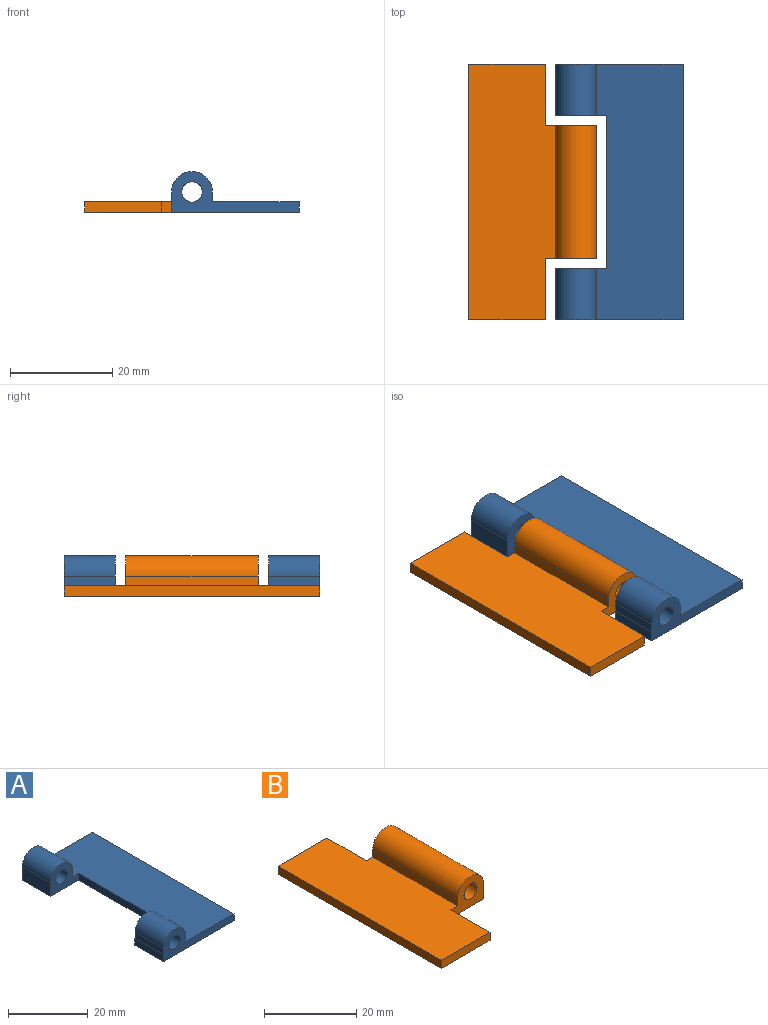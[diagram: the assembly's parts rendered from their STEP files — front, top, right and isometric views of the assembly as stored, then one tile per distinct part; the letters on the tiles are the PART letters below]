
ASSEMBLY  parts=2 mates=1
PART A: 18 faces, bbox 25x50x8 mm
  f0: plane 50x25.03mm, normal (0,0,-1), area 950.3mm2, adj f3,f5,f6,f7,f12,f13,f14,f15
  f1: plane 10x1.87mm, normal (1,0,0), area 18.6mm2, adj f2,f5,f8,f13
  f2: cylinder r=4mm len=10mm, axis (0,1,0), area 125.7mm2, adj f1,f5,f11,f13
  f3: plane 10x4mm, normal (-1,0,0), area 40mm2, adj f0,f6,f10,f12
  f4: plane 10x0.03mm, normal (0,0,1), area 0.3mm2, adj f5,f11,f13,f14
  f5: plane 25.03x8mm, normal (0,-1,0), area 80.9mm2, adj f0,f1,f2,f4,f7,f8,f11,f14
  f6: plane 25x8mm, normal (0,1,0), area 80.9mm2, adj f0,f3,f7,f8,f9,f10,f17
  f7: plane 50x2.14mm, normal (1,0,0), area 106.8mm2, adj f0,f5,f6,f8
  f8: plane 50x17mm, normal (0,0,1), area 790mm2, adj f1,f5,f6,f7,f9,f12,f13,f15
  f9: plane 10x1.87mm, normal (1,0,0), area 18.6mm2, adj f6,f8,f10,f12
  f10: cylinder r=4mm len=10mm, axis (0,1,0), area 125.7mm2, adj f3,f6,f9,f12
  f11: plane 10x1.87mm, normal (-1,0,0), area 18.6mm2, adj f2,f4,f5,f13
  f12: plane 10x8mm, normal (0,-1,0), area 48.8mm2, adj f0,f3,f8,f9,f10,f15,f17
  f13: plane 10.03x8mm, normal (0,1,0), area 48.9mm2, adj f0,f1,f2,f4,f8,f11,f14,f15
  f14: plane 10x2.14mm, normal (-1,0,0), area 21.4mm2, adj f0,f4,f5,f13
  f15: plane 30x2.14mm, normal (-1,0,0), area 64.1mm2, adj f0,f8,f12,f13
  f16: cylinder r=2mm len=10mm, axis (0,-1,0), area 125.7mm2, adj f5,f13
  f17: cylinder r=2mm len=10mm, axis (0,-1,0), area 125.7mm2, adj f6,f12
PART B: 13 faces, bbox 25x50x8 mm
  f0: plane 50x2.14mm, normal (-1,0,0), area 106.8mm2, adj f1,f2,f5,f6
  f1: plane 50x25mm, normal (0,0,-1), area 1009.6mm2, adj f0,f5,f6,f7,f8,f9,f10,f11
  f2: plane 50x17mm, normal (0,0,1), area 801.6mm2, adj f0,f3,f5,f6,f8,f9,f10,f11
  f3: plane 26x1.87mm, normal (-1,0,0), area 48.5mm2, adj f2,f4,f8,f9
  f4: cylinder r=4mm len=26mm, axis (0,1,0), area 326.7mm2, adj f3,f7,f8,f9
  f5: plane 15x2.14mm, normal (0,1,0), area 32mm2, adj f0,f1,f2,f10
  f6: plane 14.97x2.14mm, normal (0,-1,0), area 32mm2, adj f0,f1,f2,f11
  f7: plane 26x4mm, normal (1,0,0), area 104mm2, adj f1,f4,f8,f9
  f8: plane 10x8mm, normal (0,1,0), area 48.8mm2, adj f1,f2,f3,f4,f7,f10,f12
  f9: plane 10.03x8mm, normal (0,-1,0), area 48.9mm2, adj f1,f2,f3,f4,f7,f11,f12
  f10: plane 12x2.14mm, normal (1,0,0), area 25.6mm2, adj f1,f2,f5,f8
  f11: plane 12x2.14mm, normal (1,0,0), area 25.6mm2, adj f1,f2,f6,f9
  f12: cylinder r=2mm len=26mm, axis (0,-1,0), area 326.7mm2, adj f8,f9
PLACE A t=(-14.58,3.85,-0.06)mm
PLACE B t=(-14.58,3.85,-0.06)mm
MATE revolute B.f4 <-> A.f2  axis (0,-1,0) through (-41.18,-34.15,3.94)mm
